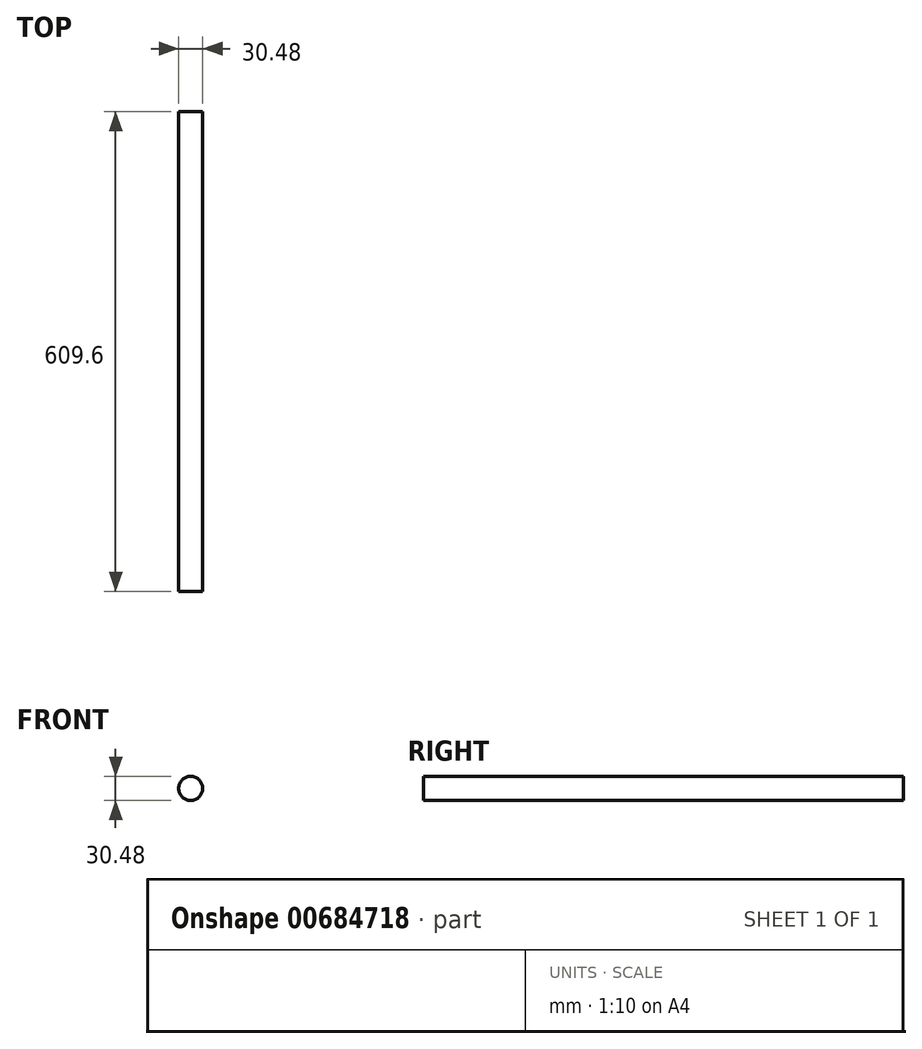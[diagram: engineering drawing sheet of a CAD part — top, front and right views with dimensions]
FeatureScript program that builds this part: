
annotation { "Feature Type Name" : "Feature", "Feature Type Description" : "" }
export const myFeature = defineFeature(function(context is Context, id is Id, definition is map)
    precondition{}
    {
        {
            var Q0;
            Q0=qCreatedBy(makeId("Front.planeOp"),FACE);
            var sketch = newSketch(context, id + "F0", { "sketchPlane" : qUnion([Q0])});
            skCircle(sketch, "E0", {"center": v(0, 0) * mm, "radius": 15.24 * mm});
            skSolve(sketch);
        }
        {
            var Q0;
            Q0 = qSketchRegion(id + "F0", true);
            extrude(context, id + "F1", {"entities" : qUnion([Q0]), "depth" : 609.6 * mm, "offsetDistance" : 30.48 * mm});
        }
    });
